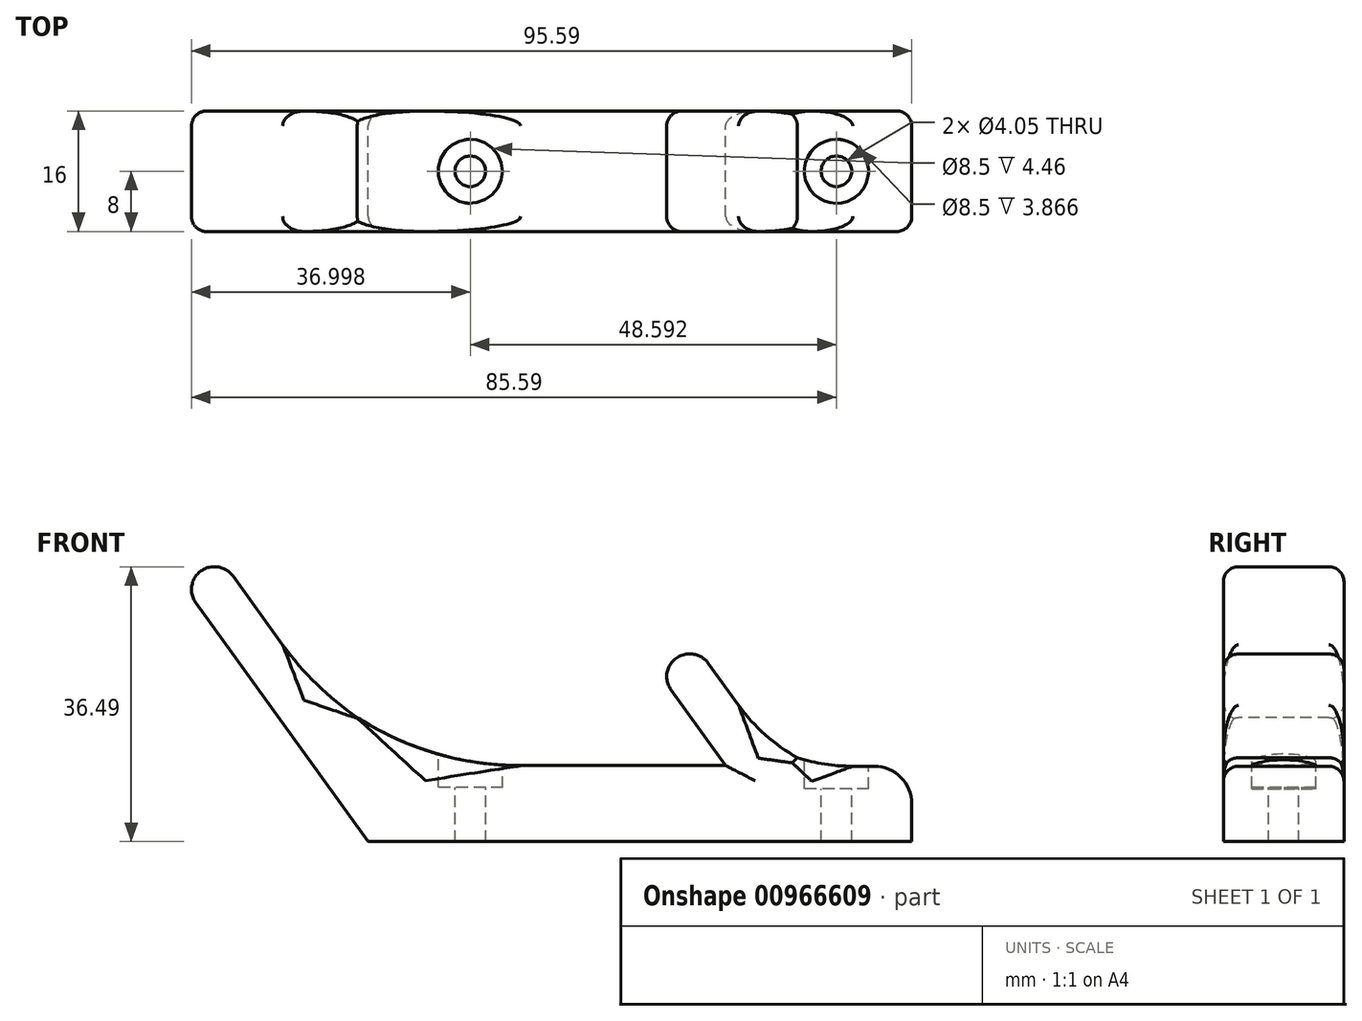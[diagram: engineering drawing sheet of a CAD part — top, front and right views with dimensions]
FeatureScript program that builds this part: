
annotation { "Feature Type Name" : "Feature", "Feature Type Description" : "" }
export const myFeature = defineFeature(function(context is Context, id is Id, definition is map)
    precondition{}
    {
        {
            var Q0;
            Q0=qCreatedBy(makeId("Front.planeOp"),FACE);
            var sketch = newSketch(context, id + "F0", { "sketchPlane" : qUnion([Q0])});
            skLineSegment(sketch, "E0", {"start": v(-34.93, 1.03) * mm, "end": v(37.21, 1.03) * mm});
            skLineSegment(sketch, "E1", {"start": v(37.21, 1.03) * mm, "end": v(37.21, 11.03) * mm});
            skLineSegment(sketch, "E2", {"start": v(37.21, 11.03) * mm, "end": v(24.35, 11.03) * mm});
            skLineSegment(sketch, "E3", {"start": v(9.3, 25.94) * mm, "end": v(1.8, 25.94) * mm});
            skLineSegment(sketch, "E4", {"start": v(1.8, 25.94) * mm, "end": v(12.51, 11.11) * mm});
            skLineSegment(sketch, "E5", {"start": v(12.51, 11.11) * mm, "end": v(-26.74, 11.11) * mm});
            skLineSegment(sketch, "E6", {"start": v(-53.76, 37.52) * mm, "end": v(-61.26, 37.52) * mm});
            skLineSegment(sketch, "E7", {"start": v(-61.26, 37.52) * mm, "end": v(-34.93, 1.03) * mm});
            skLineSegment(sketch, "E8", {"start": v(-42.03, 21.26) * mm, "end": v(-53.76, 37.52) * mm});
            skLineSegment(sketch, "E9", {"start": v(-26.74, 11.11) * mm, "end": v(-42.03, 21.26) * mm});
            skLineSegment(sketch, "E10", {"start": v(18.13, 13.72) * mm, "end": v(9.3, 25.94) * mm});
            skLineSegment(sketch, "E11", {"start": v(24.35, 11.03) * mm, "end": v(18.13, 13.72) * mm});
            skSolve(sketch);
        }
        {
            var Q0;
            Q0=makeQuery(id+"F0.imprint","IMPRINT",FACE,{"disambiguationData":[TD([[makeQuery(id+"F0.imprint","IMPRINT",EDGE,{"derivedFrom":sQuery(id+"F0.wireOp",EDGE,"E0")}),1.0]])]});
            extrude(context, id + "F1", {"entities" : qUnion([Q0]), "depth" : 16 * mm, "offsetDistance" : 25 * mm});
        }
        {
            var Q0;
            Q0=makeQuery(id+"F1.opExtrude","CAP_EDGE",EDGE,{"disambiguationData":[OSD([sQuery(id+"F0.wireOp",EDGE,"E5")])],"isStart":false});
            var Q1;
            Q1=makeQuery(id+"F1.opExtrude","CAP_EDGE",EDGE,{"disambiguationData":[OSD([sQuery(id+"F0.wireOp",EDGE,"E4")])],"isStart":false});
            var Q2;
            Q2=makeQuery(id+"F1.opExtrude","CAP_EDGE",EDGE,{"disambiguationData":[OSD([sQuery(id+"F0.wireOp",EDGE,"E3")])],"isStart":false});
            var Q3;
            Q3=makeQuery(id+"F1.opExtrude","CAP_EDGE",EDGE,{"disambiguationData":[OSD([sQuery(id+"F0.wireOp",EDGE,"E10")])],"isStart":false});
            var Q4;
            Q4=makeQuery(id+"F1.opExtrude","CAP_EDGE",EDGE,{"disambiguationData":[OSD([sQuery(id+"F0.wireOp",EDGE,"E11")])],"isStart":false});
            var Q5;
            Q5=makeQuery(id+"F1.opExtrude","CAP_EDGE",EDGE,{"disambiguationData":[OSD([sQuery(id+"F0.wireOp",EDGE,"E2")])],"isStart":false});
            var Q6;
            Q6=makeQuery(id+"F1.opExtrude","CAP_EDGE",EDGE,{"disambiguationData":[OSD([sQuery(id+"F0.wireOp",EDGE,"E1")])],"isStart":false});
            var Q7;
            Q7=makeQuery(id+"F1.opExtrude","CAP_EDGE",EDGE,{"disambiguationData":[OSD([sQuery(id+"F0.wireOp",EDGE,"E7")])],"isStart":false});
            var Q8;
            Q8=makeQuery(id+"F1.opExtrude","CAP_EDGE",EDGE,{"disambiguationData":[OSD([sQuery(id+"F0.wireOp",EDGE,"E9")])],"isStart":false});
            var Q9;
            Q9=makeQuery(id+"F1.opExtrude","CAP_EDGE",EDGE,{"disambiguationData":[OSD([sQuery(id+"F0.wireOp",EDGE,"E8")])],"isStart":false});
            var Q10;
            Q10=makeQuery(id+"F1.opExtrude","CAP_EDGE",EDGE,{"disambiguationData":[OSD([sQuery(id+"F0.wireOp",EDGE,"E6")])],"isStart":false});
            var Q11;
            Q11=makeQuery(id+"F1.opExtrude","CAP_EDGE",EDGE,{"disambiguationData":[OSD([sQuery(id+"F0.wireOp",EDGE,"E1")])],"isStart":true});
            var Q12;
            Q12=makeQuery(id+"F1.opExtrude","CAP_EDGE",EDGE,{"disambiguationData":[OSD([sQuery(id+"F0.wireOp",EDGE,"E2")])],"isStart":true});
            var Q13;
            Q13=makeQuery(id+"F1.opExtrude","CAP_EDGE",EDGE,{"disambiguationData":[OSD([sQuery(id+"F0.wireOp",EDGE,"E11")])],"isStart":true});
            var Q14;
            Q14=makeQuery(id+"F1.opExtrude","CAP_EDGE",EDGE,{"disambiguationData":[OSD([sQuery(id+"F0.wireOp",EDGE,"E10")])],"isStart":true});
            var Q15;
            Q15=makeQuery(id+"F1.opExtrude","CAP_EDGE",EDGE,{"disambiguationData":[OSD([sQuery(id+"F0.wireOp",EDGE,"E3")])],"isStart":true});
            var Q16;
            Q16=makeQuery(id+"F1.opExtrude","CAP_EDGE",EDGE,{"disambiguationData":[OSD([sQuery(id+"F0.wireOp",EDGE,"E4")])],"isStart":true});
            var Q17;
            Q17=makeQuery(id+"F1.opExtrude","CAP_EDGE",EDGE,{"disambiguationData":[OSD([sQuery(id+"F0.wireOp",EDGE,"E5")])],"isStart":true});
            var Q18;
            Q18=makeQuery(id+"F1.opExtrude","CAP_EDGE",EDGE,{"disambiguationData":[OSD([sQuery(id+"F0.wireOp",EDGE,"E9")])],"isStart":true});
            var Q19;
            Q19=makeQuery(id+"F1.opExtrude","CAP_EDGE",EDGE,{"disambiguationData":[OSD([sQuery(id+"F0.wireOp",EDGE,"E8")])],"isStart":true});
            var Q20;
            Q20=makeQuery(id+"F1.opExtrude","CAP_EDGE",EDGE,{"disambiguationData":[OSD([sQuery(id+"F0.wireOp",EDGE,"E6")])],"isStart":true});
            var Q21;
            Q21=makeQuery(id+"F1.opExtrude","CAP_EDGE",EDGE,{"disambiguationData":[OSD([sQuery(id+"F0.wireOp",EDGE,"E7")])],"isStart":true});
            fillet(context, id + "F2", {"entities" : qUnion([Q0, Q1, Q2, Q3, Q4, Q5, Q6, Q7, Q8, Q9, Q10, Q11, Q12, Q13, Q14, Q15, Q16, Q17, Q18, Q19, Q20, Q21]), "radius" : 2 * mm, "tangentPropagation" : true, "allowEdgeOverflow" : false});
        }
        {
            var Q0;
            Q0=makeQuery(id+"F1.opExtrude","SWEPT_EDGE",EDGE,{"disambiguationData":[OSD([sQuery(id+"F0.wireOp",EDGE,"E3"),sQuery(id+"F0.wireOp",EDGE,"E4")])]});
            var Q1;
            Q1=makeQuery(id+"F1.opExtrude","SWEPT_EDGE",EDGE,{"disambiguationData":[OSD([sQuery(id+"F0.wireOp",EDGE,"E3"),sQuery(id+"F0.wireOp",EDGE,"E10")])]});
            var Q2;
            Q2=makeQuery(id+"F1.opExtrude","SWEPT_EDGE",EDGE,{"disambiguationData":[OSD([sQuery(id+"F0.wireOp",EDGE,"E6"),sQuery(id+"F0.wireOp",EDGE,"E8")])]});
            var Q3;
            Q3=makeQuery(id+"F1.opExtrude","SWEPT_EDGE",EDGE,{"disambiguationData":[OSD([sQuery(id+"F0.wireOp",EDGE,"E6"),sQuery(id+"F0.wireOp",EDGE,"E7")])]});
            fillet(context, id + "F3", {"entities" : qUnion([Q0, Q1, Q2, Q3]), "radius" : 3 * mm, "tangentPropagation" : true, "allowEdgeOverflow" : false});
        }
        {
            var Q0;
            Q0=makeQuery(id+"F1.opExtrude","SWEPT_EDGE",EDGE,{"disambiguationData":[OSD([sQuery(id+"F0.wireOp",EDGE,"E8"),sQuery(id+"F0.wireOp",EDGE,"E9")])]});
            var Q1;
            Q1=makeQuery(id+"F1.opExtrude","SWEPT_FACE",FACE,{"disambiguationData":[OSD([sQuery(id+"F0.wireOp",EDGE,"E9")])]});
            var Q2;
            Q2=makeQuery(id+"F1.opExtrude","SWEPT_FACE",FACE,{"disambiguationData":[OSD([sQuery(id+"F0.wireOp",EDGE,"E8")])]});
            fillet(context, id + "F4", {"entities" : qUnion([Q0, Q1, Q2]), "radius" : 40 * mm, "tangentPropagation" : true, "allowEdgeOverflow" : false});
        }
        {
            var Q0;
            Q0=makeQuery(id+"F1.opExtrude","SWEPT_EDGE",EDGE,{"disambiguationData":[OSD([sQuery(id+"F0.wireOp",EDGE,"E2"),sQuery(id+"F0.wireOp",EDGE,"E11")])]});
            var Q1;
            Q1=makeQuery(id+"F1.opExtrude","SWEPT_EDGE",EDGE,{"disambiguationData":[OSD([sQuery(id+"F0.wireOp",EDGE,"E10"),sQuery(id+"F0.wireOp",EDGE,"E11")])]});
            fillet(context, id + "F5", {"entities" : qUnion([Q0, Q1]), "radius" : 24.24 * mm, "tangentPropagation" : true, "allowEdgeOverflow" : false});
        }
        {
            var Q0;
            Q0=makeQuery(id+"F1.opExtrude","SWEPT_EDGE",EDGE,{"disambiguationData":[OSD([sQuery(id+"F0.wireOp",EDGE,"E1"),sQuery(id+"F0.wireOp",EDGE,"E2")])]});
            fillet(context, id + "F6", {"entities" : qUnion([Q0]), "radius" : 5 * mm, "tangentPropagation" : true, "allowEdgeOverflow" : false});
        }
        {
            var Q0;
            Q0=makeQuery(id+"F1.opExtrude","SWEPT_FACE",FACE,{"disambiguationData":[OSD([sQuery(id+"F0.wireOp",EDGE,"E5")])]});
            cPlane(context, id + "F7", {"entities" : qUnion([Q0]), "cplaneType" : CPlaneType.OFFSET, "offset" : 4.7 * mm, "width" : 150 * mm, "height" : 150 * mm});
        }
        {
            var Q0;
            Q0=qCreatedBy(id+"F7.planeOp",FACE);
            var sketch = newSketch(context, id + "F8", { "sketchPlane" : qUnion([Q0])});
            skCircle(sketch, "E12", {"center": v(-21.38, -8) * mm, "radius": 2 * mm});
            skSolve(sketch);
        }
        {
            var Q0;
            Q0=sQuery(id+"F8.wireOp",VERTEX,"E12.center");
            var Q1;
            Q1=makeQuery(id+"F1.opExtrude","SWEPT_BODY",BODY,{"disambiguationData":[OSD([sQuery(id+"F0.wireOp",EDGE,"E0"),sQuery(id+"F0.wireOp",EDGE,"E1"),sQuery(id+"F0.wireOp",EDGE,"E2"),sQuery(id+"F0.wireOp",EDGE,"E3"),sQuery(id+"F0.wireOp",EDGE,"E4"),sQuery(id+"F0.wireOp",EDGE,"E5"),sQuery(id+"F0.wireOp",EDGE,"E6"),sQuery(id+"F0.wireOp",EDGE,"E7"),sQuery(id+"F0.wireOp",EDGE,"E8"),sQuery(id+"F0.wireOp",EDGE,"E9"),sQuery(id+"F0.wireOp",EDGE,"E10"),sQuery(id+"F0.wireOp",EDGE,"E11")])]});
            hole(context, id + "F9", {"style" : HoleStyle.C_BORE, "endStyle" : HoleEndStyle.THROUGH, "holeDiameter" : 4.05 * mm, "cBoreDiameter" : 8.5 * mm, "cBoreDepth" : 3 * mm, "majorDiameter" : 5 * mm, "isTappedThrough" : true, "tappedDepth" : 12 * mm, "tapClearance" : 3, "locations" : qUnion([Q0]), "scope" : qUnion([Q1])});
        }
        {
            var Q0;
            Q0=qCreatedBy(id+"F7.planeOp",FACE);
            var sketch = newSketch(context, id + "F10", { "sketchPlane" : qUnion([Q0])});
            skCircle(sketch, "E13", {"center": v(27.21, -8) * mm, "radius": 2 * mm});
            skSolve(sketch);
        }
        {
            var Q0;
            Q0=sQuery(id+"F10.wireOp",VERTEX,"E13.center");
            var Q1;
            Q1=makeQuery(id+"F1.opExtrude","SWEPT_BODY",BODY,{"disambiguationData":[OSD([sQuery(id+"F0.wireOp",EDGE,"E0"),sQuery(id+"F0.wireOp",EDGE,"E1"),sQuery(id+"F0.wireOp",EDGE,"E2"),sQuery(id+"F0.wireOp",EDGE,"E3"),sQuery(id+"F0.wireOp",EDGE,"E4"),sQuery(id+"F0.wireOp",EDGE,"E5"),sQuery(id+"F0.wireOp",EDGE,"E6"),sQuery(id+"F0.wireOp",EDGE,"E7"),sQuery(id+"F0.wireOp",EDGE,"E8"),sQuery(id+"F0.wireOp",EDGE,"E9"),sQuery(id+"F0.wireOp",EDGE,"E10"),sQuery(id+"F0.wireOp",EDGE,"E11")])]});
            hole(context, id + "F11", {"style" : HoleStyle.C_BORE, "endStyle" : HoleEndStyle.THROUGH, "holeDiameter" : 4.05 * mm, "cBoreDiameter" : 8.5 * mm, "cBoreDepth" : 3 * mm, "majorDiameter" : 5 * mm, "isTappedThrough" : true, "tappedDepth" : 12 * mm, "tapClearance" : 3, "locations" : qUnion([Q0]), "scope" : qUnion([Q1])});
        }
    });
